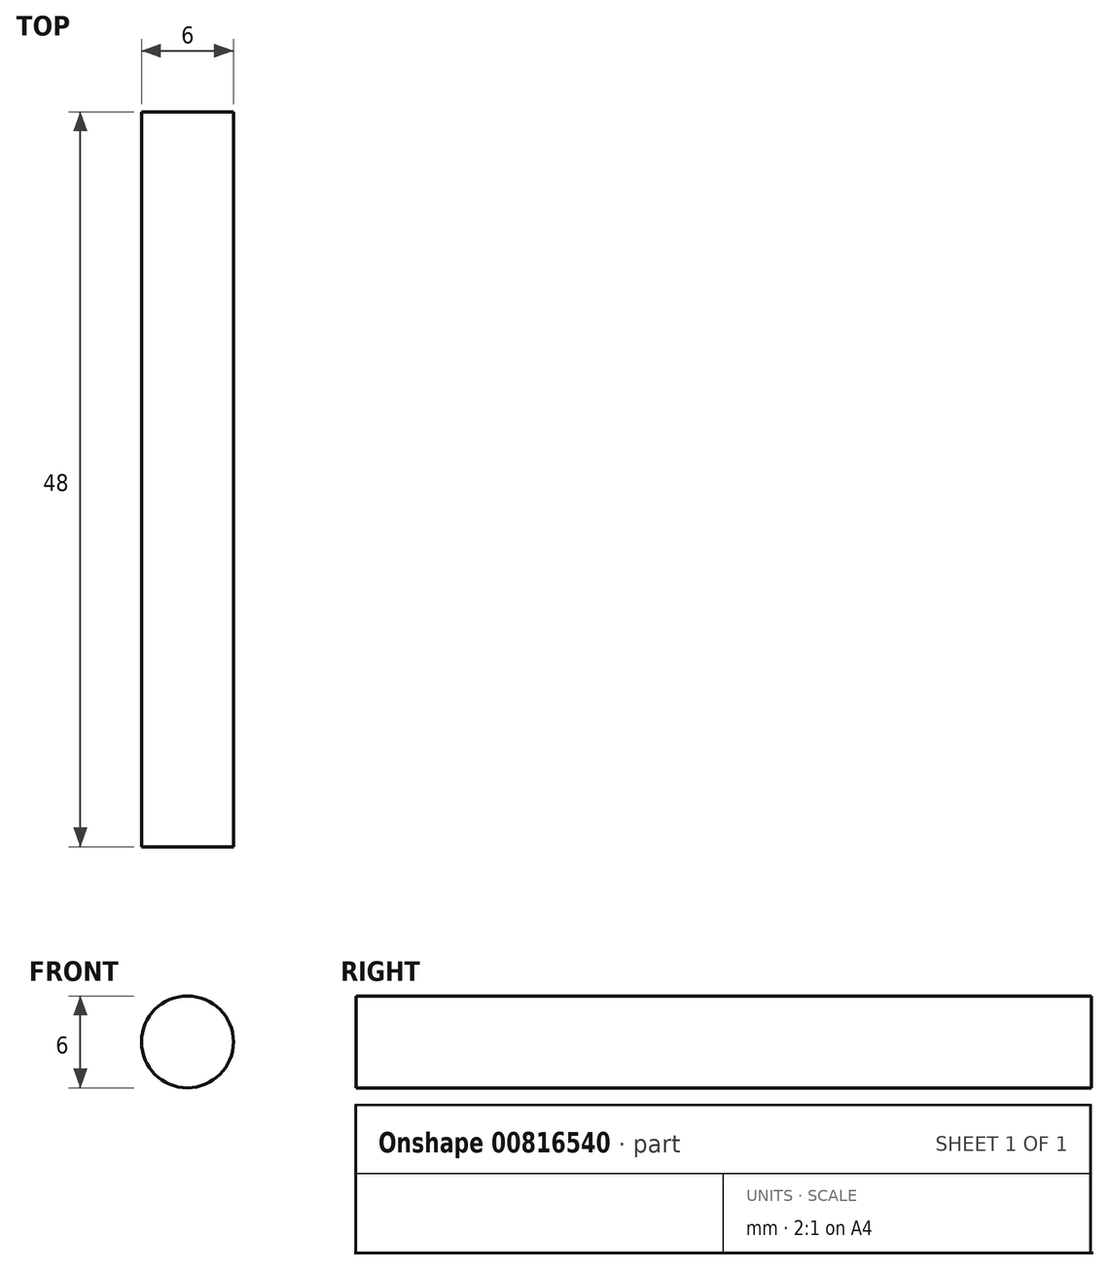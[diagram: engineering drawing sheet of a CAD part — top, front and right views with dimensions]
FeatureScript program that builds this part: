
annotation { "Feature Type Name" : "Feature", "Feature Type Description" : "" }
export const myFeature = defineFeature(function(context is Context, id is Id, definition is map)
    precondition{}
    {
        {
            assignVariable(context, id + "F0", {"name" : "Bolzenlaenge", "anyValue" : 48});
        }
        {
            var Q0;
            Q0=qCreatedBy(makeId("Front.planeOp"),FACE);
            var sketch = newSketch(context, id + "F1", { "sketchPlane" : qUnion([Q0])});
            skCircle(sketch, "E0", {"center": v(0, 0) * mm, "radius": 3 * mm});
            skSolve(sketch);
        }
        {
            var Q0;
            Q0=makeQuery(id+"F1.imprint","IMPRINT",FACE,{"disambiguationData":[TD([[makeQuery(id+"F1.imprint","IMPRINT",EDGE,{"derivedFrom":sQuery(id+"F1.wireOp",EDGE,"E0")}),1.0]])]});
            extrude(context, id + "F2", {"entities" : qUnion([Q0]), "depth" : (getVariable(context, 'Bolzenlaenge')) * mm, "offsetDistance" : 25 * mm});
        }
    });
